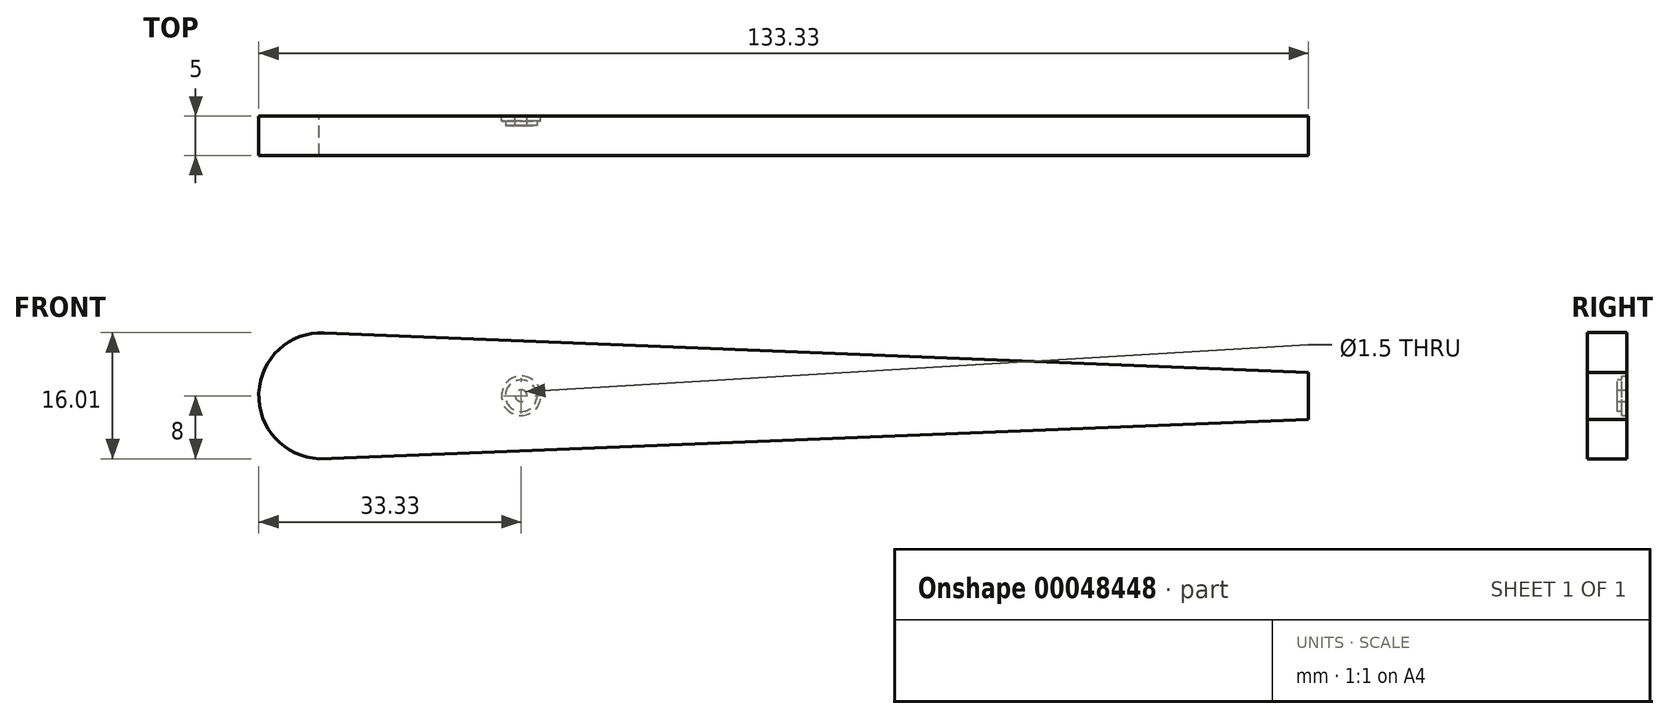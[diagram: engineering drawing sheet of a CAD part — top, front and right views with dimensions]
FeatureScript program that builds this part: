
annotation { "Feature Type Name" : "Feature", "Feature Type Description" : "" }
export const myFeature = defineFeature(function(context is Context, id is Id, definition is map)
    precondition{}
    {
        {
            var Q0;
            Q0=qCreatedBy(makeId("Front.planeOp"),FACE);
            var sketch = newSketch(context, id + "F0", { "sketchPlane" : qUnion([Q0])});
            skCircle(sketch, "E0", {"center": v(0, 0) * mm, "radius": 2.5 * mm});
            skCircle(sketch, "E1", {"center": v(0, 0) * mm, "radius": 0.75 * mm});
            skSolve(sketch);
        }
        {
            var Q0;
            Q0 = qSketchRegion(id + "F0", true);
            extrude(context, id + "F1", {"entities" : qUnion([Q0]), "depth" : 1.2 * mm});
        }
        {
            var Q0;
            Q0=makeQuery(id+"F1.opExtrude","CAP_FACE",FACE,{"disambiguationData":[OSD([sQuery(id+"F0.wireOp",EDGE,"E0"),sQuery(id+"F0.wireOp",EDGE,"E1")])],"isStart":false});
            var sketch = newSketch(context, id + "F2", { "sketchPlane" : qUnion([Q0])});
            skCircle(sketch, "E2", {"center": v(0, 0) * mm, "radius": 2 * mm});
            skCircle(sketch, "E3", {"center": v(0, 0) * mm, "radius": 4.22 * mm});
            skSolve(sketch);
        }
        {
            var Q0;
            Q0=makeQuery(id+"F2.imprint","IMPRINT",FACE,{"disambiguationData":[TD([[makeQuery(id+"F2.imprint","IMPRINT",EDGE,{"derivedFrom":sQuery(id+"F2.wireOp",EDGE,"E3")}),1.0]])]});
            var Q1;
            Q1=makeQuery(id+"F2.imprint","IMPRINT",FACE,{"disambiguationData":[TD([[makeQuery(id+"F2.imprint","IMPRINT",EDGE,{"derivedFrom":sQuery(id+"F2.wireOp",EDGE,"E2")}),-1.0]])]});
            extrude(context, id + "F3", {"entities" : qUnion([Q0, Q1]), "operationType" : NewBodyOperationType.REMOVE, "oppositeDirection" : true, "depth" : .6 * mm});
        }
        {
            var Q0;
            Q0=makeQuery(id+"F1.opExtrude","SWEPT_BODY",BODY,{"disambiguationData":[OSD([sQuery(id+"F0.wireOp",EDGE,"E0"),sQuery(id+"F0.wireOp",EDGE,"E1")])]});
            transform(context, id + "F4", {"entities" : qUnion([Q0]), "transformType" : TransformType.TRANSLATION_3D, "dx" : 0 * mm, "dy" : 0 * mm, "dz" : 0 * mm, "makeCopy" : true});
        }
        {
            var Q0;
            Q0=qCreatedBy(makeId("Front.planeOp"),FACE);
            var sketch = newSketch(context, id + "F5", { "sketchPlane" : qUnion([Q0])});
            skLineSegment(sketch, "E4", {"start": v(-25, 8) * mm, "end": v(100, 2.96) * mm});
            skLineSegment(sketch, "E5", {"start": v(100, 2.96) * mm, "end": v(100, -3) * mm});
            skLineSegment(sketch, "E6", {"start": v(100, -3) * mm, "end": v(-25.64, -8) * mm});
            skLineSegment(sketch, "E7", {"start": v(-68.84, 0) * mm, "end": v(92.63, 0) * mm, "construction": true});
            skLineSegment(sketch, "E8", {"start": v(0, 51.02) * mm, "end": v(0, -39.85) * mm, "construction": true});
            skArc(sketch, "E9", {"start": v(-25, 8) * mm, "mid": v(-33.32, 0.32) * mm, "end": v(-25.64, -8) * mm});
            skSolve(sketch);
        }
        {
            var Q0;
            Q0=makeQuery(id+"F5.imprint","IMPRINT",FACE,{"disambiguationData":[TD([[makeQuery(id+"F5.imprint","IMPRINT",EDGE,{"derivedFrom":sQuery(id+"F5.wireOp",EDGE,"E4")}),-1.0]])]});
            extrude(context, id + "F6", {"entities" : qUnion([Q0]), "depth" : 5 * mm});
        }
        {
            var Q0;
            Q0=makeQuery(id+"F4.opPattern","COPY",BODY,{"derivedFrom":makeQuery(id+"F1.opExtrude","SWEPT_BODY",BODY,{"disambiguationData":[OSD([sQuery(id+"F0.wireOp",EDGE,"E0"),sQuery(id+"F0.wireOp",EDGE,"E1")])]}),"instanceName":"1"});
            deleteBodies(context, id + "F7", {"entities" : qUnion([Q0])});
        }
    });
